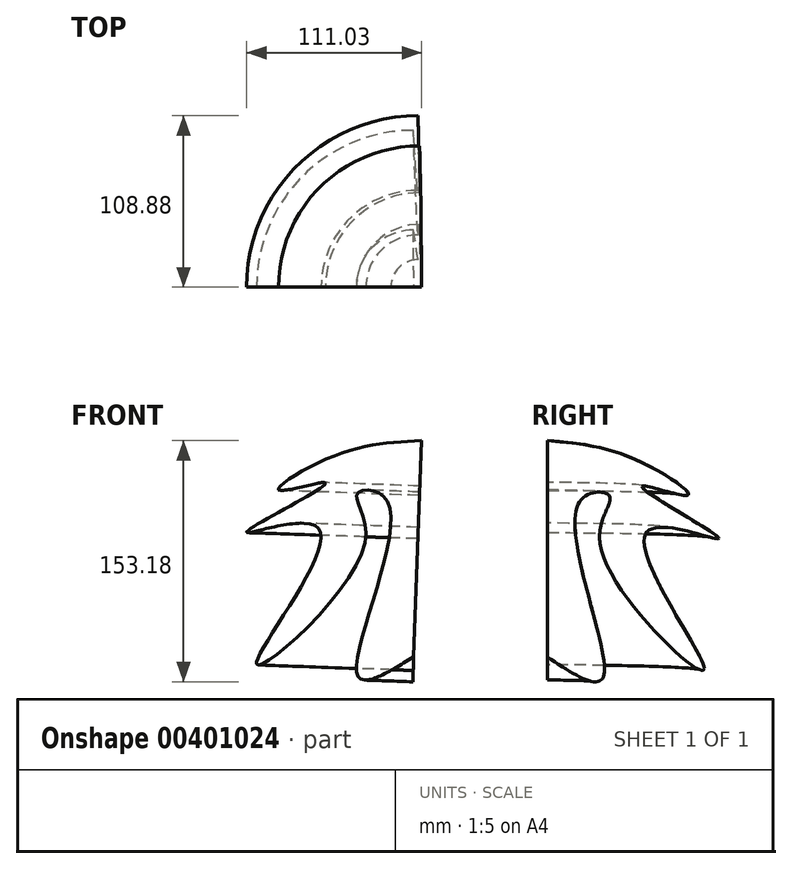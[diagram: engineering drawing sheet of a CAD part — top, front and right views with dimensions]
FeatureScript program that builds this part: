
annotation { "Feature Type Name" : "Feature", "Feature Type Description" : "" }
export const myFeature = defineFeature(function(context is Context, id is Id, definition is map)
    precondition{}
    {
        {
            var Q0;
            Q0=qCreatedBy(makeId("Front.planeOp"),FACE);
            var sketch = newSketch(context, id + "F0", { "sketchPlane" : qUnion([Q0])});
            skLineSegment(sketch, "E0", {"start": v(-25.03, 73.5) * mm, "end": v(-29.96, -64) * mm});
            skFitSpline(sketch, "E1", {"points": [v(-25.03, 73.5) * mm, v(-83.54, 62.6) * mm, v(-114.91, 41.9) * mm, v(-86, 46.38) * mm, v(-136.06, 15.36) * mm, v(-90.24, 17.66) * mm, v(-129.72, -68.11) * mm, v(-61.33, 6.62) * mm, v(-65.56, 39.94) * mm, v(-46.18, 33.9) * mm, v(-65.92, -75.07) * mm, v(-29.96, -64) * mm], "startDerivative": vector(-574.04, -28.13) * mm, "endDerivative": vector(648.83, 395.52) * mm});
            skSolve(sketch);
        }
        {
            var Q0;
            Q0=makeQuery(id+"F0.imprint","IMPRINT",FACE,{"disambiguationData":[TD([[makeQuery(id+"F0.imprint","IMPRINT",EDGE,{"derivedFrom":sQuery(id+"F0.wireOp",EDGE,"E0")}),-1.0]])]});
            var Q1;
            Q1=sQuery(id+"F0.wireOp",EDGE,"E0");
            revolve(context, id + "F1", {"entities" : qUnion([Q0]), "axis" : qUnion([Q1]), "revolveType" : RevolveType.ONE_DIRECTION, "angle" : 90 * degree});
        }
    });
